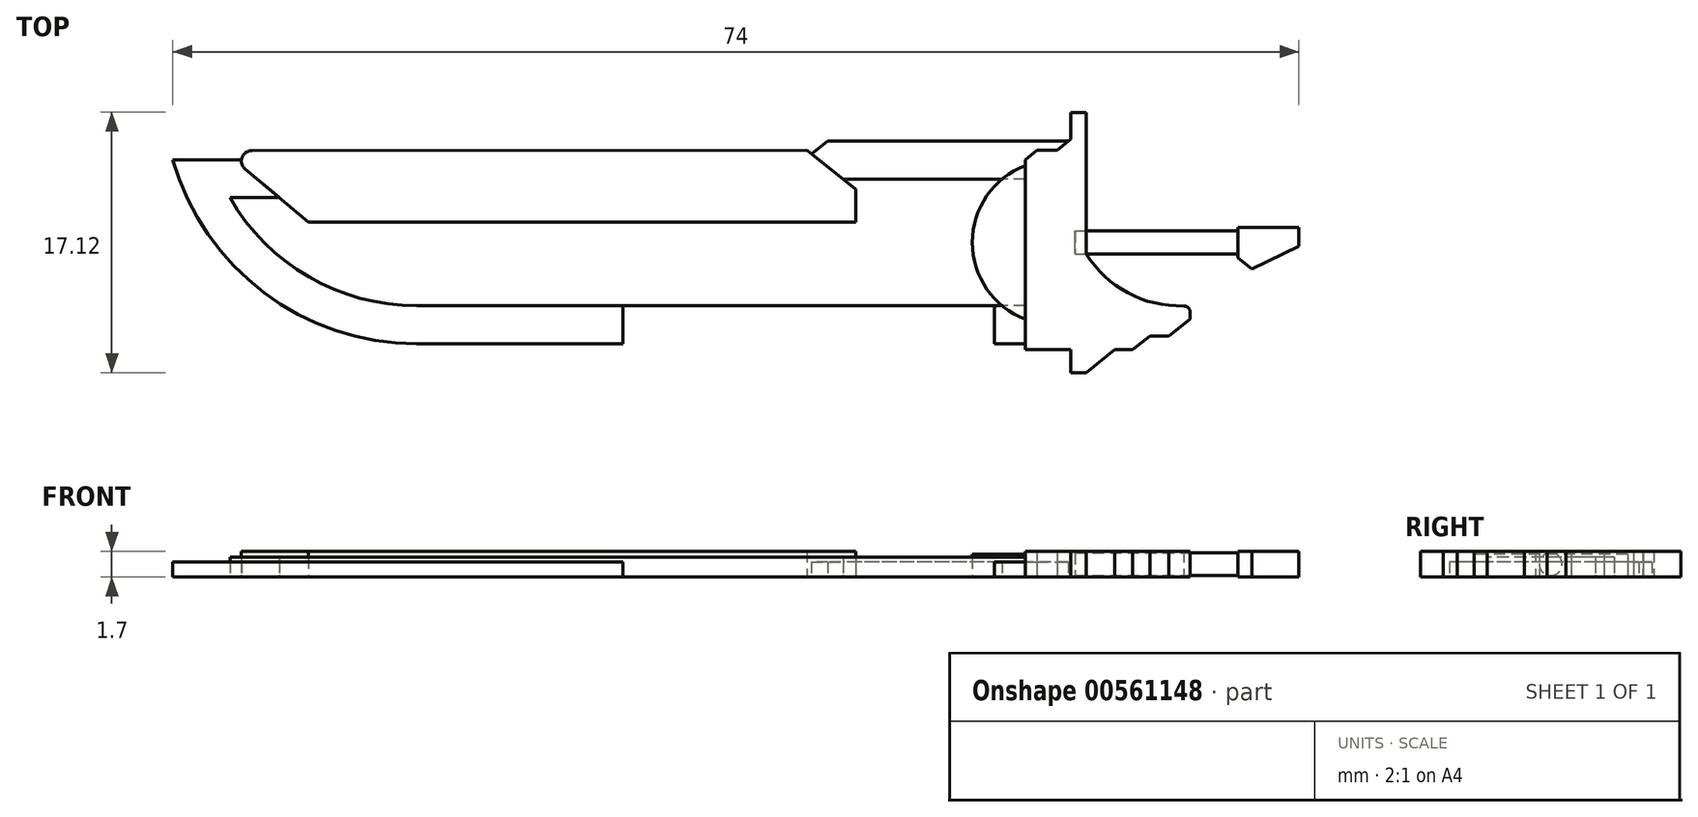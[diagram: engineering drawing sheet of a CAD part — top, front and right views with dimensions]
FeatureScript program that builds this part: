
annotation { "Feature Type Name" : "Feature", "Feature Type Description" : "" }
export const myFeature = defineFeature(function(context is Context, id is Id, definition is map)
    precondition{}
    {
        {
            var Q0;
            Q0=qCreatedBy(makeId("Top.planeOp"),FACE);
            var sketch = newSketch(context, id + "F0", { "sketchPlane" : qUnion([Q0])});
            skLineSegment(sketch, "E0", {"start": v(-17.33, -2.03) * mm, "end": v(-17.33, -14.53) * mm});
            skLineSegment(sketch, "E1", {"start": v(-17.33, -14.53) * mm, "end": v(-13.33, -14.53) * mm});
            skLineSegment(sketch, "E2", {"start": v(-13.33, -14.53) * mm, "end": v(-13.33, -0.41) * mm});
            skLineSegment(sketch, "E3", {"start": v(-13.33, -0.41) * mm, "end": v(-13.99, -0.41) * mm});
            skPoint(sketch, "E4.start.orphan", {"position": v(-13.33, -7.47) * mm});
            skLineSegment(sketch, "E5", {"start": v(-13.33, -14.53) * mm, "end": v(-10.3, -14.53) * mm});
            skLineSegment(sketch, "E6", {"start": v(-10.3, -14.53) * mm, "end": v(-9.15, -13.62) * mm});
            skLineSegment(sketch, "E7", {"start": v(-9.15, -13.62) * mm, "end": v(-7.9, -13.62) * mm});
            skLineSegment(sketch, "E8", {"start": v(-7.9, -13.62) * mm, "end": v(-6.5, -12.5) * mm});
            skLineSegment(sketch, "E9", {"start": v(-6.5, -12.5) * mm, "end": v(-6.5, -12.04) * mm});
            skPoint(sketch, "E10.visualSharp", {"position": v(-6.5, -11.6) * mm});
            skArc(sketch, "E10.filletArc", {"start": v(-6.5, -12.04) * mm, "mid": v(-6.63, -11.75) * mm, "end": v(-6.93, -11.64) * mm});
            skCircle(sketch, "E11", {"center": v(-53, 58.34) * mm, "radius": 11.76 * mm});
            skLineSegment(sketch, "E12", {"start": v(-53, 70.1) * mm, "end": v(-53, 46.59) * mm});
            skLineSegment(sketch, "E13", {"start": v(-17.33, -2.03) * mm, "end": v(-16.55, -1.4) * mm});
            skLineSegment(sketch, "E14", {"start": v(-16.55, -1.4) * mm, "end": v(-15.24, -1.4) * mm});
            skLineSegment(sketch, "E15", {"start": v(-15.24, -1.4) * mm, "end": v(-13.99, -0.41) * mm});
            skLineSegment(sketch, "E16", {"start": v(-3.36, 1.88) * mm, "end": v(-73.36, 1.88) * mm});
            skLineSegment(sketch, "E17", {"start": v(-17.33, -14.13) * mm, "end": v(-43.77, -14.13) * mm});
            skLineSegment(sketch, "E18.MirrorCS", {"start": v(-17.33, -2.03) * mm, "end": v(-18.12, -1.4) * mm});
            skLineSegment(sketch, "E19", {"start": v(-14.5, -0.81) * mm, "end": v(-30.3, -0.81) * mm});
            skLineSegment(sketch, "E20", {"start": v(-30.3, -0.81) * mm, "end": v(-31.83, -2.03) * mm});
            skLineSegment(sketch, "E21", {"start": v(-31.83, -2.03) * mm, "end": v(-57.33, -2.03) * mm});
            skLineSegment(sketch, "E22", {"start": v(-13.33, -7.47) * mm, "end": v(-17.33, -7.47) * mm});
            skLineSegment(sketch, "E23", {"start": v(-43.77, -2.03) * mm, "end": v(-43.77, -14.13) * mm});
            skLineSegment(sketch, "E24", {"start": v(-43.77, -8.08) * mm, "end": v(-46.21, -8.08) * mm});
            skPoint(sketch, "E24.endSnap0", {"position": v(-43.77, -8.08) * mm});
            skLineSegment(sketch, "E25.MirrorCS", {"start": v(-31.83, -14.13) * mm, "end": v(-43.77, -14.13) * mm});
            skLineSegment(sketch, "E26", {"start": v(-43.77, -14.13) * mm, "end": v(-57.33, -14.13) * mm});
            skLineSegment(sketch, "E27", {"start": v(-57.33, -2.03) * mm, "end": v(-73.36, -2.03) * mm});
            skArc(sketch, "E28", {"start": v(-73.36, -2.03) * mm, "mid": v(-67.37, -10.76) * mm, "end": v(-57.33, -14.13) * mm});
            skLineSegment(sketch, "E29", {"start": v(-64.14, -6.13) * mm, "end": v(-55.48, -6.13) * mm});
            skLineSegment(sketch, "E30", {"start": v(-55.48, -6.13) * mm, "end": v(-50.32, -2.03) * mm});
            skLineSegment(sketch, "E31", {"start": v(-55.48, -6.13) * mm, "end": v(-37, -6.13) * mm});
            skLineSegment(sketch, "E32", {"start": v(-19.37, -0.81) * mm, "end": v(-19.37, -14.13) * mm});
            skLineSegment(sketch, "E33", {"start": v(-18.69, -0.81) * mm, "end": v(-18.69, -2.41) * mm});
            skLineSegment(sketch, "E34", {"start": v(-18.56, -14.13) * mm, "end": v(-18.56, -12.53) * mm});
            skPoint(sketch, "E35", {"position": v(-17.33, -12.53) * mm});
            skPoint(sketch, "E36", {"position": v(-17.33, -2.41) * mm});
            skArc(sketch, "E37", {"start": v(-17.33, -2.41) * mm, "mid": v(-20.81, -7.47) * mm, "end": v(-17.33, -12.53) * mm});
            skLineSegment(sketch, "E38", {"start": v(-13.33, -7.47) * mm, "end": v(-11.3, -7.47) * mm});
            skLineSegment(sketch, "E39", {"start": v(-3.36, -6.72) * mm, "end": v(-11.43, -6.72) * mm});
            skLineSegment(sketch, "E40.MirrorCS", {"start": v(-3.36, -8.22) * mm, "end": v(-11.43, -8.22) * mm});
            skLineSegment(sketch, "E41", {"start": v(0.64, -6.72) * mm, "end": v(0.64, -7.72) * mm});
            skLineSegment(sketch, "E42", {"start": v(0.64, -7.72) * mm, "end": v(-2.23, -9.11) * mm});
            skLineSegment(sketch, "E43", {"start": v(-6.5, -12.5) * mm, "end": v(-6.5, -14.5) * mm});
            skLineSegment(sketch, "E44.MirrorCS", {"start": v(-5.1, -13.62) * mm, "end": v(-6.5, -12.5) * mm});
            skLineSegment(sketch, "E45", {"start": v(0.64, 1.88) * mm, "end": v(-3.36, 1.88) * mm});
            skLineSegment(sketch, "E46", {"start": v(0.64, 3.29) * mm, "end": v(-73.36, 3.29) * mm});
            skLineSegment(sketch, "E47", {"start": v(-34.55, -3.98) * mm, "end": v(-37, -2.03) * mm});
            skLineSegment(sketch, "E48", {"start": v(-34.55, -6.13) * mm, "end": v(-37, -6.13) * mm});
            skLineSegment(sketch, "E49", {"start": v(-50.32, -2.03) * mm, "end": v(-49.86, -1.67) * mm});
            skLineSegment(sketch, "E50", {"start": v(-49.86, -1.67) * mm, "end": v(-67.91, -1.67) * mm});
            skLineSegment(sketch, "E51", {"start": v(-37, -2.03) * mm, "end": v(-37.45, -1.67) * mm});
            skLineSegment(sketch, "E52", {"start": v(-37.45, -1.67) * mm, "end": v(-49.86, -1.67) * mm});
            skLineSegment(sketch, "E53", {"start": v(-34.55, -6.13) * mm, "end": v(-34.55, -3.98) * mm});
            skPoint(sketch, "E54.visualSharp", {"position": v(-69.02, -1.67) * mm});
            skPoint(sketch, "E55.end.orphan", {"position": v(-68.43, -2.72) * mm});
            skLineSegment(sketch, "E56", {"start": v(-37.45, -1.67) * mm, "end": v(-31.38, -1.67) * mm});
            skLineSegment(sketch, "E57", {"start": v(-31.38, -1.67) * mm, "end": v(-28.47, -3.98) * mm});
            skLineSegment(sketch, "E58", {"start": v(-28.47, -3.98) * mm, "end": v(-28.47, -6.13) * mm});
            skLineSegment(sketch, "E59", {"start": v(-28.47, -6.13) * mm, "end": v(-34.96, -6.13) * mm});
            skLineSegment(sketch, "E60", {"start": v(-31.38, -1.67) * mm, "end": v(-31.7, -1.42) * mm});
            skLineSegment(sketch, "E61", {"start": v(-31.7, -1.42) * mm, "end": v(-68.15, -1.42) * mm});
            skPoint(sketch, "E62.visualSharp", {"position": v(-70.08, -1.42) * mm});
            skArc(sketch, "E62.filletArc", {"start": v(-68.15, -1.42) * mm, "mid": v(-68.8, -1.88) * mm, "end": v(-68.6, -2.66) * mm});
            skLineSegment(sketch, "E63", {"start": v(-68.6, -2.66) * mm, "end": v(-64.44, -6.13) * mm});
            skLineSegment(sketch, "E64", {"start": v(-64.44, -6.13) * mm, "end": v(-64.14, -6.13) * mm});
            skLineSegment(sketch, "E65", {"start": v(-11.43, -6.72) * mm, "end": v(-13.33, -6.72) * mm});
            skLineSegment(sketch, "E66", {"start": v(-11.43, -8.22) * mm, "end": v(-13.33, -8.22) * mm});
            skArc(sketch, "E67.0", {"start": v(-13.2, -8.43) * mm, "mid": v(-12.37, -7.4) * mm, "end": v(-13.33, -6.5) * mm});
            skLineSegment(sketch, "E68", {"start": v(-11.3, -7.47) * mm, "end": v(-5.92, -7.47) * mm});
            skPoint(sketch, "E69.MirrorCS.end.orphan", {"position": v(-3.36, -8.22) * mm});
            skLineSegment(sketch, "E70", {"start": v(-3.36, -8.22) * mm, "end": v(-3.36, -6.72) * mm});
            skLineSegment(sketch, "E71", {"start": v(-5.92, -7.47) * mm, "end": v(-3.36, -7.47) * mm});
            skArc(sketch, "E72", {"start": v(-13.33, -8.22) * mm, "mid": v(-10.59, -10.78) * mm, "end": v(-6.93, -11.64) * mm});
            skArc(sketch, "E73.trimOffspring", {"start": v(-11.43, -6.72) * mm, "mid": v(-11.3, -7.47) * mm, "end": v(-11.43, -8.22) * mm});
            skPoint(sketch, "E74.start.orphan", {"position": v(-15.38, -7.47) * mm});
            skLineSegment(sketch, "E75", {"start": v(-3.36, -7.47) * mm, "end": v(-3.36, -6.72) * mm});
            skLineSegment(sketch, "E76", {"start": v(-3.36, -7.47) * mm, "end": v(-3.36, -6.47) * mm});
            skLineSegment(sketch, "E77", {"start": v(-3.36, -7.47) * mm, "end": v(-3.36, -8.47) * mm});
            skLineSegment(sketch, "E78", {"start": v(-3.36, -8.47) * mm, "end": v(-2.43, -9.2) * mm});
            skLineSegment(sketch, "E79", {"start": v(-2.23, -9.11) * mm, "end": v(-2.43, -9.2) * mm});
            skLineSegment(sketch, "E80", {"start": v(-3.36, -6.47) * mm, "end": v(0.64, -6.47) * mm});
            skLineSegment(sketch, "E81", {"start": v(0.64, -6.47) * mm, "end": v(0.64, -6.72) * mm});
            skPoint(sketch, "E82.orphan", {"position": v(-2.23, -9.36) * mm});
            skLineSegment(sketch, "E83.0", {"start": v(-31.83, -11.63) * mm, "end": v(-43.77, -11.63) * mm});
            skLineSegment(sketch, "E83.1", {"start": v(-43.77, -11.63) * mm, "end": v(-57.33, -11.63) * mm});
            skArc(sketch, "E83.2", {"start": v(-69.6, -4.53) * mm, "mid": v(-64.42, -9.72) * mm, "end": v(-57.33, -11.63) * mm});
            skLineSegment(sketch, "E83.3", {"start": v(-57.33, -4.53) * mm, "end": v(-69.6, -4.53) * mm});
            skLineSegment(sketch, "E84.0", {"start": v(-29.43, -3.31) * mm, "end": v(-30.28, -3.98) * mm});
            skLineSegment(sketch, "E84.1", {"start": v(-14.5, -3.31) * mm, "end": v(-29.43, -3.31) * mm});
            skLineSegment(sketch, "E85", {"start": v(-31.83, -11.63) * mm, "end": v(-17.33, -11.63) * mm});
            skLineSegment(sketch, "E86", {"start": v(-57.33, -4.53) * mm, "end": v(-30.28, -3.98) * mm});
            skPoint(sketch, "E87.orphan", {"position": v(-13.33, 0) * mm});
            skLineSegment(sketch, "E88", {"start": v(-14.34, 0.69) * mm, "end": v(-14.34, -0.69) * mm});
            skLineSegment(sketch, "E89", {"start": v(-13.33, -0.41) * mm, "end": v(-13.33, 0.69) * mm});
            skPoint(sketch, "E90.end.orphan", {"position": v(-13.99, 0.69) * mm});
            skLineSegment(sketch, "E91", {"start": v(-13.33, 0.69) * mm, "end": v(-13.33, 1.09) * mm});
            skLineSegment(sketch, "E92", {"start": v(-13.33, 1.09) * mm, "end": v(-14.34, 1.09) * mm});
            skLineSegment(sketch, "E93", {"start": v(-14.34, 1.09) * mm, "end": v(-14.34, 0.69) * mm});
            skLineSegment(sketch, "E94.MirrorCS", {"start": v(-13.33, -16.03) * mm, "end": v(-14.34, -16.03) * mm});
            skLineSegment(sketch, "E95.MirrorCS", {"start": v(-14.34, -15.63) * mm, "end": v(-14.34, -14.25) * mm});
            skLineSegment(sketch, "E96.MirrorCS", {"start": v(-14.34, -16.03) * mm, "end": v(-14.34, -15.63) * mm});
            skLineSegment(sketch, "E97", {"start": v(-13.33, -16.03) * mm, "end": v(-11.45, -14.53) * mm});
            skPoint(sketch, "E98.MirrorCS.end.orphan", {"position": v(-13.33, -15.63) * mm});
            skPoint(sketch, "E98.MirrorCS.start.orphan", {"position": v(-13.33, -14.53) * mm});
            skPoint(sketch, "E99.MirrorCS.end.orphan", {"position": v(-13.33, -16.03) * mm});
            skLineSegment(sketch, "E100", {"start": v(5.63, 1.09) * mm, "end": v(5.63, -16.03) * mm});
            skLineSegment(sketch, "E101", {"start": v(-14.34, 4.18) * mm, "end": v(-73.36, 4.18) * mm});
            skLineSegment(sketch, "E102", {"start": v(-13.33, -0.41) * mm, "end": v(-13.33, -14.53) * mm});
            skSolve(sketch);
        }
        {
            var Q0;
            Q0=makeQuery(id+"F0.imprint","IMPRINT",FACE,{"disambiguationData":[TD([[makeQuery(id+"F0.imprint","IMPRINT",EDGE,{"derivedFrom":sQuery(id+"F0.wireOp",EDGE,"E29")}),1.0]])]});
            var Q1;
            {var subQ0=sQuery(id+"F0.wireOp",EDGE,"E49");Q1=makeQuery(id+"F0.imprint","IMPRINT",FACE,{"disambiguationData":[TD([[makeQuery(id+"F0.imprint","IMPRINT",EDGE,{"derivedFrom":subQ0}),1.0]])]});}
            var Q2;
            {var subQ3=sQuery(id+"F0.wireOp",EDGE,"E30");Q2=makeQuery(id+"F0.imprint","IMPRINT",FACE,{"disambiguationData":[TD([[makeQuery(id+"F0.imprint","IMPRINT",EDGE,{"derivedFrom":subQ3}),-1.0]])]});}
            var Q3;
            {var subQ0=sQuery(id+"F0.wireOp",EDGE,"E47");Q3=makeQuery(id+"F0.imprint","IMPRINT",FACE,{"disambiguationData":[TD([[makeQuery(id+"F0.imprint","IMPRINT",EDGE,{"derivedFrom":subQ0}),1.0]])]});}
            var Q4;
            {var subQ1=sQuery(id+"F0.wireOp",EDGE,"E49");Q4=makeQuery(id+"F0.imprint","IMPRINT",FACE,{"disambiguationData":[TD([[makeQuery(id+"F0.imprint","IMPRINT",EDGE,{"derivedFrom":subQ1}),-1.0]])]});}
            var Q5;
            {var subQ1=sQuery(id+"F0.wireOp",EDGE,"E47");Q5=makeQuery(id+"F0.imprint","IMPRINT",FACE,{"disambiguationData":[TD([[makeQuery(id+"F0.imprint","IMPRINT",EDGE,{"derivedFrom":subQ1}),-1.0]])]});}
            var Q6;
            {var subQ4=sQuery(id+"F0.wireOp",EDGE,"E51");Q6=makeQuery(id+"F0.imprint","IMPRINT",FACE,{"disambiguationData":[TD([[makeQuery(id+"F0.imprint","IMPRINT",EDGE,{"derivedFrom":subQ4}),-1.0]])]});}
            var Q7;
            {var subQ3=sQuery(id+"F0.wireOp",EDGE,"E27");var subQ6=sQuery(id+"F0.wireOp",EDGE,"E21");var subQ12=makeQuery(id+"F0.imprint","INTERSECT",VERTEX,{"derivedFrom":[subQ6,subQ3]});Q7=makeQuery(id+"F0.imprint","IMPRINT",FACE,{"disambiguationData":[TD([[makeQuery(id+"F0.imprint","IMPRINT",EDGE,{"disambiguationData":[TD([[subQ12,-1.0]])],"derivedFrom":subQ3}),1.0]])]});}
            var Q8;
            {var subQ0=sQuery(id+"F0.wireOp",EDGE,"E48");Q8=makeQuery(id+"F0.imprint","IMPRINT",FACE,{"disambiguationData":[TD([[makeQuery(id+"F0.imprint","IMPRINT",EDGE,{"derivedFrom":subQ0}),-1.0]])]});}
            var Q9;
            {var subQ3=sQuery(id+"F0.wireOp",EDGE,"E58");Q9=makeQuery(id+"F0.imprint","IMPRINT",FACE,{"disambiguationData":[TD([[makeQuery(id+"F0.imprint","IMPRINT",EDGE,{"derivedFrom":subQ3}),-1.0]])]});}
            extrude(context, id + "F1", {"entities" : qUnion([Q0, Q1, Q2, Q3, Q4, Q5, Q6, Q7, Q8, Q9]), "depth" : 1.7 * mm, "offsetDistance" : 25 * mm});
        }
        {
            var Q0;
            {var subQ0=sQuery(id+"F0.wireOp",EDGE,"E26");Q0=makeQuery(id+"F0.imprint","IMPRINT",FACE,{"disambiguationData":[TD([[makeQuery(id+"F0.imprint","IMPRINT",EDGE,{"derivedFrom":subQ0}),-1.0]])]});}
            var Q1;
            {var subQ8=sQuery(id+"F0.wireOp",EDGE,"E25.MirrorCS");Q1=makeQuery(id+"F0.imprint","IMPRINT",FACE,{"disambiguationData":[TD([[makeQuery(id+"F0.imprint","IMPRINT",EDGE,{"derivedFrom":subQ8}),-1.0]])]});}
            var Q2;
            {var subQ4=sQuery(id+"F0.wireOp",EDGE,"E13");Q2=makeQuery(id+"F0.imprint","IMPRINT",FACE,{"disambiguationData":[TD([[makeQuery(id+"F0.imprint","IMPRINT",EDGE,{"derivedFrom":subQ4}),1.0]])]});}
            var Q3;
            {var subQ1=sQuery(id+"F0.wireOp",EDGE,"E17");var subQ5=makeQuery(id+"F0.imprint","IMPRINT",VERTEX,{"derivedFrom":subQ1});Q3=makeQuery(id+"F0.imprint","IMPRINT",FACE,{"disambiguationData":[TD([[makeQuery(id+"F0.imprint","IMPRINT",EDGE,{"disambiguationData":[TD([[subQ5,1.0]])],"derivedFrom":subQ1}),-1.0]])]});}
            var Q4;
            {var subQ1=sQuery(id+"F0.wireOp",EDGE,"E20");var subQ6=sQuery(id+"F0.wireOp",EDGE,"E19");var subQ9=makeQuery(id+"F0.imprint","INTERSECT",VERTEX,{"derivedFrom":[subQ6,subQ1]});Q4=makeQuery(id+"F0.imprint","IMPRINT",FACE,{"disambiguationData":[TD([[makeQuery(id+"F0.imprint","IMPRINT",EDGE,{"disambiguationData":[TD([[subQ9,1.0]])],"derivedFrom":subQ6}),1.0]])]});}
            extrude(context, id + "F2", {"entities" : qUnion([Q0, Q1, Q2, Q3, Q4]), "depth" : 1 * mm, "offsetDistance" : 25 * mm});
        }
        {
            var Q0;
            {var subQ0=sQuery(id+"F0.wireOp",EDGE,"E29");Q0=makeQuery(id+"F0.imprint","IMPRINT",FACE,{"disambiguationData":[TD([[makeQuery(id+"F0.imprint","IMPRINT",EDGE,{"derivedFrom":subQ0}),-1.0]])]});}
            var Q1;
            {var subQ8=sQuery(id+"F0.wireOp",EDGE,"E48");Q1=makeQuery(id+"F0.imprint","IMPRINT",FACE,{"disambiguationData":[TD([[makeQuery(id+"F0.imprint","IMPRINT",EDGE,{"derivedFrom":subQ8}),1.0]])]});}
            var Q2;
            {var subQ0=sQuery(id+"F0.wireOp",EDGE,"E37");var subQ1=sQuery(id+"F0.wireOp",EDGE,"E32");var subQ2=makeQuery(id+"F0.imprint","INTERSECT",VERTEX,{"disambiguationData":[OD(1.0)],"derivedFrom":[subQ1,subQ0]});Q2=makeQuery(id+"F0.imprint","IMPRINT",FACE,{"disambiguationData":[TD([[makeQuery(id+"F0.imprint","IMPRINT",EDGE,{"disambiguationData":[TD([[subQ2,-1.0]])],"derivedFrom":subQ1}),1.0]])]});}
            var Q3;
            {var subQ0=sQuery(id+"F0.wireOp",EDGE,"E84.1");var subQ1=sQuery(id+"F0.wireOp",EDGE,"E32");var subQ2=makeQuery(id+"F0.imprint","INTERSECT",VERTEX,{"derivedFrom":[subQ1,subQ0]});Q3=makeQuery(id+"F0.imprint","IMPRINT",FACE,{"disambiguationData":[TD([[makeQuery(id+"F0.imprint","IMPRINT",EDGE,{"disambiguationData":[TD([[subQ2,-1.0]])],"derivedFrom":subQ1}),1.0]])]});}
            var Q4;
            {var subQ6=sQuery(id+"F0.wireOp",EDGE,"E0");var subQ7=makeQuery(id+"F0.imprint","INTERSECT",VERTEX,{"derivedFrom":[subQ6,sQuery(id+"F0.wireOp",EDGE,"E22")]});Q4=makeQuery(id+"F0.imprint","IMPRINT",FACE,{"disambiguationData":[TD([[makeQuery(id+"F0.imprint","IMPRINT",EDGE,{"disambiguationData":[TD([[subQ7,1.0]])],"derivedFrom":subQ6}),-1.0]])]});}
            var Q5;
            {var subQ0=sQuery(id+"F0.wireOp",EDGE,"E37");var subQ1=sQuery(id+"F0.wireOp",EDGE,"E32");var subQ2=makeQuery(id+"F0.imprint","INTERSECT",VERTEX,{"disambiguationData":[OD(0.0)],"derivedFrom":[subQ1,subQ0]});Q5=makeQuery(id+"F0.imprint","IMPRINT",FACE,{"disambiguationData":[TD([[makeQuery(id+"F0.imprint","IMPRINT",EDGE,{"disambiguationData":[TD([[subQ2,-1.0]])],"derivedFrom":subQ1}),-1.0]])]});}
            extrude(context, id + "F3", {"entities" : qUnion([Q0, Q1, Q2, Q3, Q4, Q5]), "depth" : 1.3 * mm, "offsetDistance" : 25 * mm});
        }
        {
            var Q0;
            {var subQ6=sQuery(id+"F0.wireOp",EDGE,"E0");var subQ7=makeQuery(id+"F0.imprint","INTERSECT",VERTEX,{"derivedFrom":[subQ6,sQuery(id+"F0.wireOp",EDGE,"E22")]});Q0=makeQuery(id+"F0.imprint","IMPRINT",FACE,{"disambiguationData":[TD([[makeQuery(id+"F0.imprint","IMPRINT",EDGE,{"disambiguationData":[TD([[subQ7,1.0]])],"derivedFrom":subQ6}),-1.0]])]});}
            var Q1;
            {var subQ0=sQuery(id+"F0.wireOp",EDGE,"E37");var subQ1=sQuery(id+"F0.wireOp",EDGE,"E0");var subQ2=makeQuery(id+"F0.imprint","INTERSECT",VERTEX,{"disambiguationData":[OD(0.0)],"derivedFrom":[subQ1,subQ0]});Q1=makeQuery(id+"F0.imprint","IMPRINT",FACE,{"disambiguationData":[TD([[makeQuery(id+"F0.imprint","IMPRINT",EDGE,{"disambiguationData":[TD([[subQ2,-1.0]])],"derivedFrom":subQ1}),-1.0]])]});}
            var Q2;
            {var subQ0=sQuery(id+"F0.wireOp",EDGE,"E37");var subQ1=sQuery(id+"F0.wireOp",EDGE,"E32");var subQ2=makeQuery(id+"F0.imprint","INTERSECT",VERTEX,{"disambiguationData":[OD(0.0)],"derivedFrom":[subQ1,subQ0]});Q2=makeQuery(id+"F0.imprint","IMPRINT",FACE,{"disambiguationData":[TD([[makeQuery(id+"F0.imprint","IMPRINT",EDGE,{"disambiguationData":[TD([[subQ2,-1.0]])],"derivedFrom":subQ1}),-1.0]])]});}
            var Q3;
            {var subQ0=sQuery(id+"F0.wireOp",EDGE,"E37");var subQ1=sQuery(id+"F0.wireOp",EDGE,"E0");var subQ2=makeQuery(id+"F0.imprint","INTERSECT",VERTEX,{"disambiguationData":[OD(1.0)],"derivedFrom":[subQ1,subQ0]});Q3=makeQuery(id+"F0.imprint","IMPRINT",FACE,{"disambiguationData":[TD([[makeQuery(id+"F0.imprint","IMPRINT",EDGE,{"disambiguationData":[TD([[subQ2,1.0]])],"derivedFrom":subQ1}),-1.0]])]});}
            extrude(context, id + "F4", {"entities" : qUnion([Q0, Q1, Q2, Q3]), "depth" : 1.5 * mm, "offsetDistance" : 25 * mm});
        }
        {
            var Q0;
            {var subQ5=sQuery(id+"F0.wireOp",EDGE,"E3");Q0=makeQuery(id+"F0.imprint","IMPRINT",FACE,{"disambiguationData":[TD([[makeQuery(id+"F0.imprint","IMPRINT",EDGE,{"derivedFrom":subQ5}),1.0]])]});}
            var Q1;
            {var subQ2=sQuery(id+"F0.wireOp",EDGE,"E3");Q1=makeQuery(id+"F0.imprint","IMPRINT",FACE,{"disambiguationData":[TD([[makeQuery(id+"F0.imprint","IMPRINT",EDGE,{"derivedFrom":subQ2}),-1.0]])]});}
            var Q2;
            {var subQ6=sQuery(id+"F0.wireOp",EDGE,"E22");Q2=makeQuery(id+"F0.imprint","IMPRINT",FACE,{"disambiguationData":[TD([[makeQuery(id+"F0.imprint","IMPRINT",EDGE,{"derivedFrom":subQ6}),1.0]])]});}
            var Q3;
            Q3=makeQuery(id+"F0.imprint","IMPRINT",FACE,{"disambiguationData":[TD([[makeQuery(id+"F0.imprint","IMPRINT",EDGE,{"derivedFrom":sQuery(id+"F0.wireOp",EDGE,"E94.MirrorCS")}),-1.0]])]});
            var Q4;
            {var subQ0=sQuery(id+"F0.wireOp",EDGE,"E6");Q4=makeQuery(id+"F0.imprint","IMPRINT",FACE,{"disambiguationData":[TD([[makeQuery(id+"F0.imprint","IMPRINT",EDGE,{"derivedFrom":subQ0}),1.0]])]});}
            extrude(context, id + "F5", {"entities" : qUnion([Q0, Q1, Q2, Q3, Q4]), "depth" : 1.7 * mm, "offsetDistance" : 25 * mm});
        }
        {
            var Q0;
            Q0=makeQuery(id+"F0.imprint","IMPRINT",FACE,{"disambiguationData":[TD([[makeQuery(id+"F0.imprint","IMPRINT",EDGE,{"derivedFrom":sQuery(id+"F0.wireOp",EDGE,"E41")}),-1.0]])]});
            extrude(context, id + "F6", {"entities" : qUnion([Q0]), "depth" : 1.7 * mm, "offsetDistance" : 25 * mm});
        }
        {
            var Q0;
            Q0=makeQuery(id+"F6.opExtrude","SWEPT_FACE",FACE,{"disambiguationData":[OSD([sQuery(id+"F0.wireOp",EDGE,"E76"),sQuery(id+"F0.wireOp",EDGE,"E77")])]});
            var sketch = newSketch(context, id + "F7", { "sketchPlane" : qUnion([Q0])});
            skLineSegment(sketch, "E103", {"start": v(7.47, 0) * mm, "end": v(7.47, 1.7) * mm});
            skPoint(sketch, "E104.center.orphan", {"position": v(7.47, 0.85) * mm});
            skCircle(sketch, "E105", {"center": v(7.47, 0.85) * mm, "radius": 0.75 * mm});
            skSolve(sketch);
        }
        {
            var Q0;
            {var subQ0=sQuery(id+"F7.wireOp",EDGE,"E105");var subQ1=sQuery(id+"F7.wireOp",EDGE,"E103");var subQ2=makeQuery(id+"F7.imprint","INTERSECT",VERTEX,{"disambiguationData":[OD(0.0)],"derivedFrom":[subQ1,subQ0]});Q0=makeQuery(id+"F7.imprint","IMPRINT",FACE,{"disambiguationData":[TD([[makeQuery(id+"F7.imprint","IMPRINT",EDGE,{"disambiguationData":[TD([[subQ2,-1.0]])],"derivedFrom":subQ1}),1.0]])]});}
            var Q1;
            {var subQ0=sQuery(id+"F7.wireOp",EDGE,"E105");var subQ1=sQuery(id+"F7.wireOp",EDGE,"E103");var subQ2=makeQuery(id+"F7.imprint","INTERSECT",VERTEX,{"disambiguationData":[OD(0.0)],"derivedFrom":[subQ1,subQ0]});Q1=makeQuery(id+"F7.imprint","IMPRINT",FACE,{"disambiguationData":[TD([[makeQuery(id+"F7.imprint","IMPRINT",EDGE,{"disambiguationData":[TD([[subQ2,-1.0]])],"derivedFrom":subQ1}),-1.0]])]});}
            extrude(context, id + "F8", {"entities" : qUnion([Q0, Q1]), "depth" : 10.7 * mm, "offsetDistance" : 25 * mm});
        }
    });
